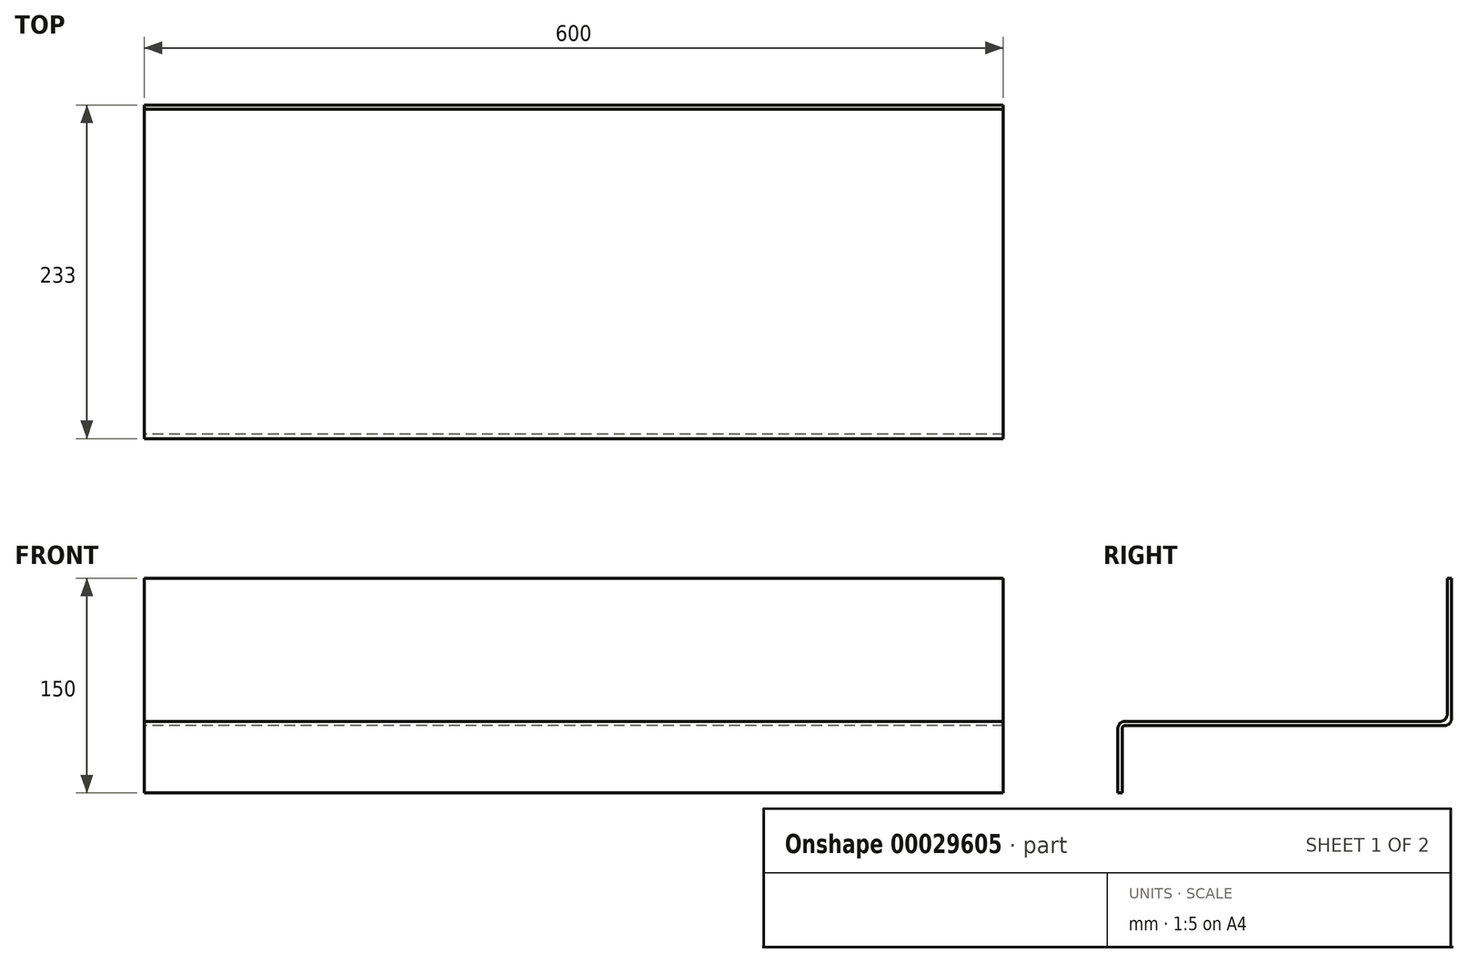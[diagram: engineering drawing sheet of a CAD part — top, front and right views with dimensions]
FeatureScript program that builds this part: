
annotation { "Feature Type Name" : "Feature", "Feature Type Description" : "" }
export const myFeature = defineFeature(function(context is Context, id is Id, definition is map)
    precondition{}
    {
        {
            var Q0;
            Q0=qCreatedBy(makeId("Right.planeOp"),FACE);
            var sketch = newSketch(context, id + "F0", { "sketchPlane" : qUnion([Q0])});
            skLineSegment(sketch, "E0", {"start": v(-207.16, 0) * mm, "end": v(12.84, 0) * mm});
            skLineSegment(sketch, "E1", {"start": v(17.84, 5) * mm, "end": v(17.84, 100) * mm});
            skLineSegment(sketch, "E2", {"start": v(-212.16, -5) * mm, "end": v(-212.16, -50) * mm});
            skLineSegment(sketch, "E3.0", {"start": v(20.84, 2) * mm, "end": v(20.84, 100) * mm});
            skLineSegment(sketch, "E3.1", {"start": v(-207.16, -3) * mm, "end": v(15.84, -3) * mm});
            skLineSegment(sketch, "E3.2", {"start": v(-209.16, -5) * mm, "end": v(-209.16, -50) * mm});
            skLineSegment(sketch, "E4", {"start": v(17.84, 100) * mm, "end": v(20.84, 100) * mm});
            skLineSegment(sketch, "E5", {"start": v(-212.16, -50) * mm, "end": v(-209.16, -50) * mm});
            skPoint(sketch, "E6.visualSharp", {"position": v(17.84, 0) * mm});
            skArc(sketch, "E6.filletArc", {"start": v(12.84, 0) * mm, "mid": v(16.37, 1.46) * mm, "end": v(17.84, 5) * mm});
            skPoint(sketch, "E7.visualSharp", {"position": v(20.84, -3) * mm});
            skArc(sketch, "E7.filletArc", {"start": v(15.84, -3) * mm, "mid": v(19.37, -1.54) * mm, "end": v(20.84, 2) * mm});
            skPoint(sketch, "E8.visualSharp", {"position": v(-209.16, -3) * mm});
            skArc(sketch, "E8.filletArc", {"start": v(-207.16, -3) * mm, "mid": v(-208.58, -3.59) * mm, "end": v(-209.16, -5) * mm});
            skPoint(sketch, "E9.visualSharp", {"position": v(-212.16, 0) * mm});
            skArc(sketch, "E9.filletArc", {"start": v(-207.16, 0) * mm, "mid": v(-210.7, -1.46) * mm, "end": v(-212.16, -5) * mm});
            skSolve(sketch);
        }
        {
            var Q0;
            Q0=makeQuery(id+"F0.imprint","IMPRINT",FACE,{"disambiguationData":[TD([[makeQuery(id+"F0.imprint","IMPRINT",EDGE,{"derivedFrom":sQuery(id+"F0.wireOp",EDGE,"E0")}),-1.0]])]});
            extrude(context, id + "F1", {"entities" : qUnion([Q0]), "depth" : 600 * mm});
        }
    });
